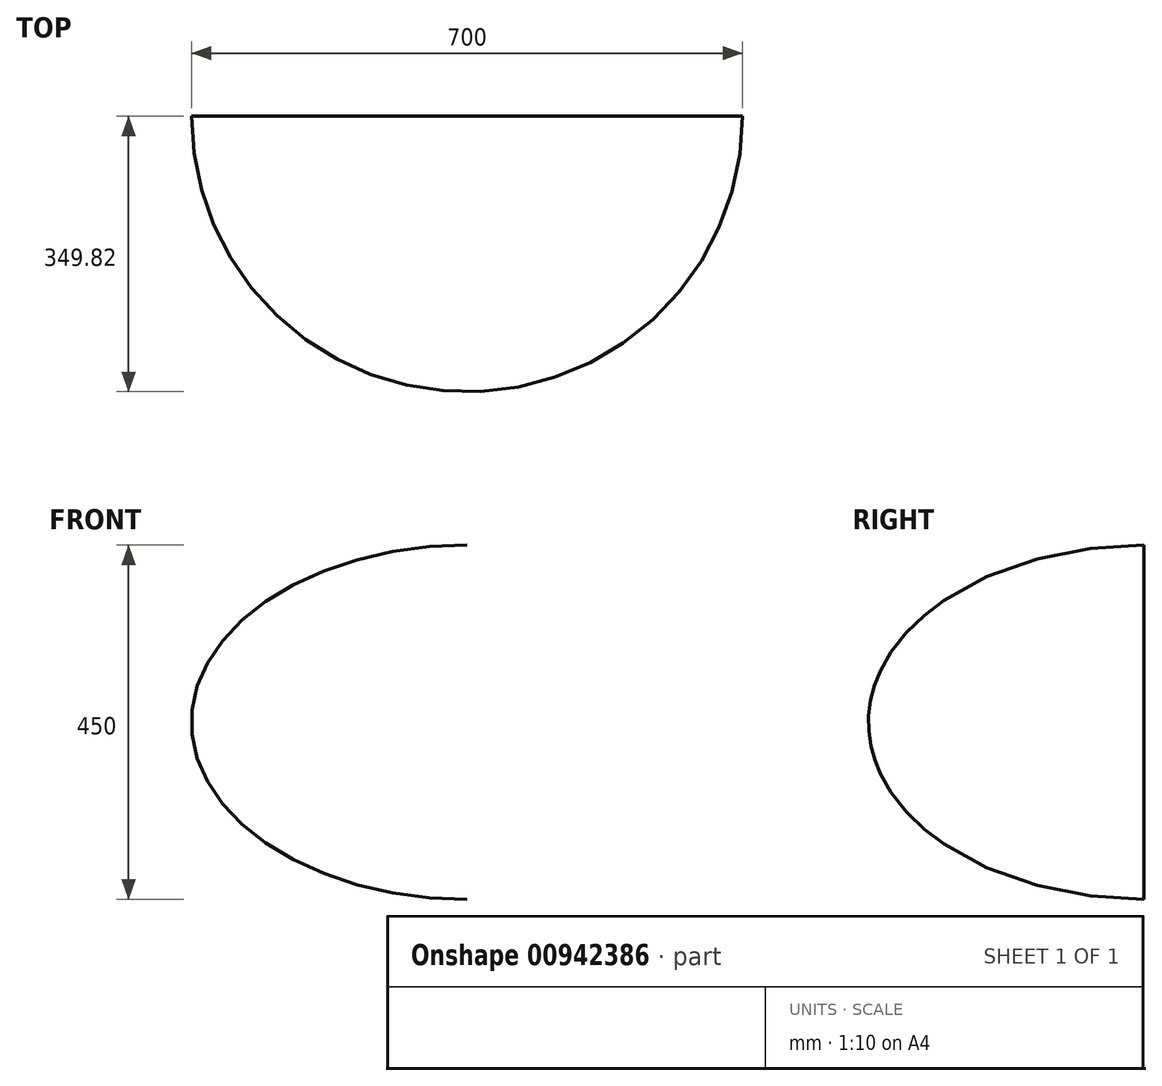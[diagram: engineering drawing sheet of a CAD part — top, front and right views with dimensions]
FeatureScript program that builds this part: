
annotation { "Feature Type Name" : "Feature", "Feature Type Description" : "" }
export const myFeature = defineFeature(function(context is Context, id is Id, definition is map)
    precondition{}
    {
        {
            var Q0;
            Q0=qCreatedBy(makeId("Front.planeOp"),FACE);
            var sketch = newSketch(context, id + "F0", { "sketchPlane" : qUnion([Q0])});
            skEllipticalArc(sketch, "E0", {});
            skLineSegment(sketch, "E1", {"start": v(0, 225) * mm, "end": v(0, -225) * mm});
            const initialGuessF0  = {"E0": [0, 0, -1, 0, 0.35, 0.225, 4.71238898038469, 1.5707963267948966]};
            skSetInitialGuess(sketch, initialGuessF0);
            skSolve(sketch);
        }
        {
            var Q0;
            Q0=makeQuery(id+"F0.imprint","IMPRINT",FACE,{"disambiguationData":[TD([[makeQuery(id+"F0.imprint","IMPRINT",EDGE,{"derivedFrom":sQuery(id+"F0.wireOp",EDGE,"E0")}),1.0]])]});
            var Q1;
            Q1=sQuery(id+"F0.wireOp",EDGE,"E1");
            revolve(context, id + "F1", {"surfaceOperationType" : NewSurfaceOperationType.NEW, "entities" : qUnion([Q0]), "axis" : qUnion([Q1]), "revolveType" : RevolveType.ONE_DIRECTION, "oppositeDirection" : true, "angle" : 180 * degree});
        }
    });
